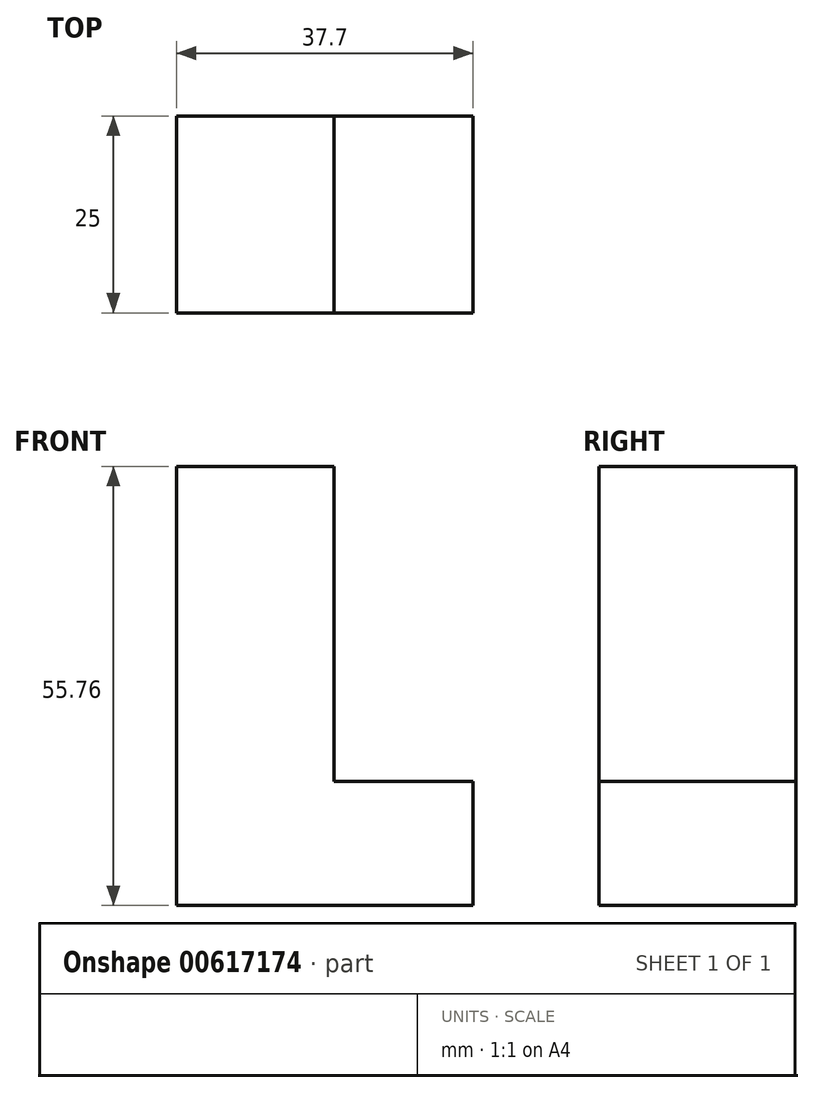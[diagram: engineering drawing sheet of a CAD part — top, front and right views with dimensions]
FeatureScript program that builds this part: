
annotation { "Feature Type Name" : "Feature", "Feature Type Description" : "" }
export const myFeature = defineFeature(function(context is Context, id is Id, definition is map)
    precondition{}
    {
        {
            var Q0;
            Q0=qCreatedBy(makeId("Front.planeOp"),FACE);
            var sketch = newSketch(context, id + "F0", { "sketchPlane" : qUnion([Q0])});
            skLineSegment(sketch, "E0", {"start": v(-59.8, 67.33) * mm, "end": v(-39.8, 67.33) * mm});
            skLineSegment(sketch, "E1", {"start": v(-59.8, 67.33) * mm, "end": v(-59.8, 11.57) * mm});
            skLineSegment(sketch, "E2", {"start": v(-39.8, 67.33) * mm, "end": v(-39.8, 27.33) * mm});
            skLineSegment(sketch, "E3", {"start": v(-39.8, 27.33) * mm, "end": v(-22.1, 27.33) * mm});
            skLineSegment(sketch, "E4", {"start": v(-22.1, 27.33) * mm, "end": v(-22.1, 11.57) * mm});
            skLineSegment(sketch, "E5", {"start": v(-59.8, 11.57) * mm, "end": v(-22.1, 11.57) * mm});
            skSolve(sketch);
        }
        {
            var Q0;
            Q0 = qSketchRegion(id + "F0", true);
            extrude(context, id + "F1", {"entities" : qUnion([Q0]), "depth" : 25 * mm, "offsetDistance" : 25 * mm});
        }
    });
